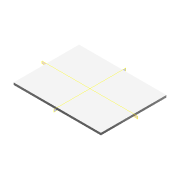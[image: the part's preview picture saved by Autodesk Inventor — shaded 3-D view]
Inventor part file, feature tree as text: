
AUTODESK INVENTOR PART (.ipt)
format: ipt  version: 2022 (Build 260153000, 153)  size: 95,744 bytes
history: native  units: in
note: dims shown in document units (in); Inventor stores cm internally (conversion verified against a paired STEP export)
features: plane x2, extrude x1, sketch x1
ambient origin geometry x8: Origin, YZ Plane, XZ Plane, XY Plane, X Axis, Y Axis, Z Axis, Center Point
bodies: Volumenkörper1 (feature_tree)
feature tree (4):
  extrude  "Extrusion1"  Depth=1.1811in
  plane  "Arbeitsebene1"
  plane  "Arbeitsebene2"
  sketch  "Skizze1"  dims[d0=1.5748in d1=1.1811in d2=0.0394in d3=0.0in]
